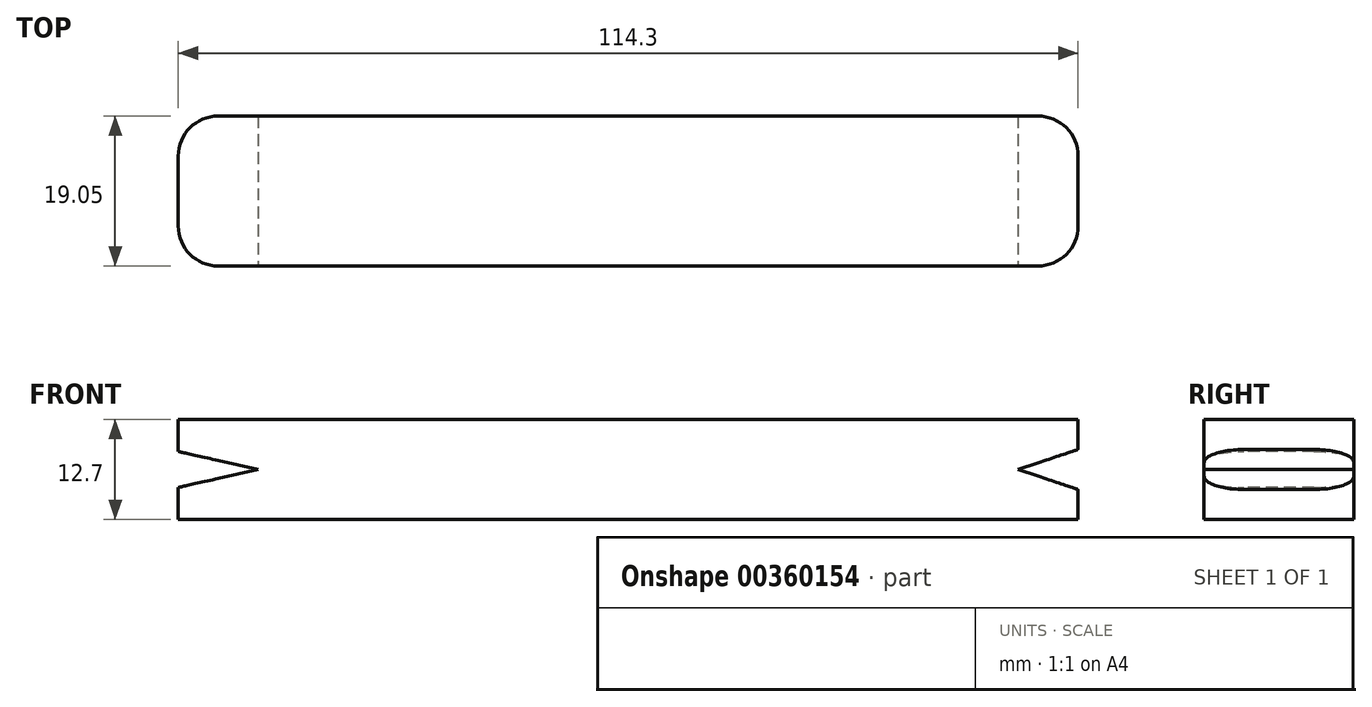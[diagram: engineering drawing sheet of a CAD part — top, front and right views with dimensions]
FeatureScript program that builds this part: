
annotation { "Feature Type Name" : "Feature", "Feature Type Description" : "" }
export const myFeature = defineFeature(function(context is Context, id is Id, definition is map)
    precondition{}
    {
        {
            var Q0;
            Q0=qCreatedBy(makeId("Front.planeOp"),FACE);
            var sketch = newSketch(context, id + "F0", { "sketchPlane" : qUnion([Q0])});
            skLineSegment(sketch, "E0.bottom", {"start": v(0, 0) * mm, "end": v(114.3, 0) * mm});
            skLineSegment(sketch, "E0.top", {"start": v(0, 12.7) * mm, "end": v(114.3, 12.7) * mm});
            skLineSegment(sketch, "E0.left", {"start": v(0, 0) * mm, "end": v(0, 12.7) * mm});
            skLineSegment(sketch, "E0.right", {"start": v(114.3, 0) * mm, "end": v(114.3, 12.7) * mm});
            skLineSegment(sketch, "E1", {"start": v(0, 6.35) * mm, "end": v(114.3, 6.35) * mm, "construction": true});
            skSolve(sketch);
        }
        {
            var Q0;
            Q0=makeQuery(id+"F0.imprint","IMPRINT",FACE,{"disambiguationData":[TD([[makeQuery(id+"F0.imprint","IMPRINT",EDGE,{"derivedFrom":sQuery(id+"F0.wireOp",EDGE,"E0.bottom")}),1.0]])]});
            extrude(context, id + "F1", {"entities" : qUnion([Q0]), "oppositeDirection" : true, "depth" : 19.05 * mm});
        }
        {
            var Q0;
            Q0=makeQuery(id+"F1.opExtrude","CAP_FACE",FACE,{"disambiguationData":[OSD([sQuery(id+"F0.wireOp",EDGE,"E0.bottom"),sQuery(id+"F0.wireOp",EDGE,"E0.top"),sQuery(id+"F0.wireOp",EDGE,"E0.left"),sQuery(id+"F0.wireOp",EDGE,"E0.right")])],"isStart":true});
            var sketch = newSketch(context, id + "F2", { "sketchPlane" : qUnion([Q0])});
            skLineSegment(sketch, "E2", {"start": v(0, 12.7) * mm, "end": v(0, 8.64) * mm, "construction": true});
            skLineSegment(sketch, "E3", {"start": v(0, 0) * mm, "end": v(0, 4.06) * mm, "construction": true});
            skLineSegment(sketch, "E4", {"start": v(0, 6.35) * mm, "end": v(10.16, 6.35) * mm, "construction": true});
            skLineSegment(sketch, "E5", {"start": v(0, 8.64) * mm, "end": v(10.16, 6.35) * mm});
            skLineSegment(sketch, "E6", {"start": v(0, 4.06) * mm, "end": v(10.16, 6.35) * mm});
            skLineSegment(sketch, "E7", {"start": v(114.3, 12.7) * mm, "end": v(114.3, 8.9) * mm, "construction": true});
            skLineSegment(sketch, "E8", {"start": v(114.3, 0) * mm, "end": v(114.3, 3.81) * mm, "construction": true});
            skLineSegment(sketch, "E9", {"start": v(114.3, 6.35) * mm, "end": v(106.68, 6.35) * mm, "construction": true});
            skLineSegment(sketch, "E10", {"start": v(114.3, 8.9) * mm, "end": v(106.68, 6.35) * mm});
            skLineSegment(sketch, "E11", {"start": v(114.3, 3.8) * mm, "end": v(106.68, 6.35) * mm});
            skSolve(sketch);
        }
        {
            var Q0;
            Q0=makeQuery(id+"F1.opExtrude","CAP_EDGE",EDGE,{"disambiguationData":[OSD([sQuery(id+"F0.wireOp",EDGE,"E0.left")])],"isStart":true});
            fillet(context, id + "F3", {"entities" : qUnion([Q0]), "radius" : 5.08 * mm, "tangentPropagation" : true, "allowEdgeOverflow" : false});
        }
        {
            var Q0;
            {var subQ0=sQuery(id+"F2.wireOp",EDGE,"E5");Q0=makeQuery(id+"F2.imprint","IMPRINT",FACE,{"disambiguationData":[TD([[makeQuery(id+"F2.imprint","IMPRINT",EDGE,{"derivedFrom":subQ0}),-1.0]])]});}
            extrude(context, id + "F4", {"entities" : qUnion([Q0]), "operationType" : NewBodyOperationType.REMOVE, "oppositeDirection" : true, "depth" : 19.05 * mm});
        }
        {
            var Q0;
            {var subQ0=sQuery(id+"F0.wireOp",EDGE,"E0.left");var subQ1=sQuery(id+"F0.wireOp",EDGE,"E0.top");Q0=makeQuery(id+"F4.boolean.opBoolean","SPLIT",EDGE,{"disambiguationData":[TD([makeQuery(id+"F1.opExtrude","SWEPT_FACE",FACE,{"disambiguationData":[OSD([subQ1])]})])],"derivedFrom":makeQuery(id+"F1.opExtrude","CAP_EDGE",EDGE,{"disambiguationData":[OSD([subQ0])],"isStart":false})});}
            var Q1;
            {var subQ0=sQuery(id+"F0.wireOp",EDGE,"E0.bottom");var subQ1=sQuery(id+"F0.wireOp",EDGE,"E0.left");Q1=makeQuery(id+"F4.boolean.opBoolean","SPLIT",EDGE,{"disambiguationData":[TD([makeQuery(id+"F1.opExtrude","SWEPT_FACE",FACE,{"disambiguationData":[OSD([subQ0])]})])],"derivedFrom":makeQuery(id+"F1.opExtrude","CAP_EDGE",EDGE,{"disambiguationData":[OSD([subQ1])],"isStart":false})});}
            fillet(context, id + "F5", {"entities" : qUnion([Q0, Q1]), "radius" : 5.08 * mm, "tangentPropagation" : true, "allowEdgeOverflow" : false});
        }
        {
            var Q0;
            Q0=makeQuery(id+"F1.opExtrude","CAP_FACE",FACE,{"disambiguationData":[OSD([sQuery(id+"F0.wireOp",EDGE,"E0.bottom"),sQuery(id+"F0.wireOp",EDGE,"E0.top"),sQuery(id+"F0.wireOp",EDGE,"E0.left"),sQuery(id+"F0.wireOp",EDGE,"E0.right")])],"isStart":true});
            var sketch = newSketch(context, id + "F6", { "sketchPlane" : qUnion([Q0])});
            skLineSegment(sketch, "E12", {"start": v(114.3, 12.7) * mm, "end": v(114.3, 8.9) * mm, "construction": true});
            skLineSegment(sketch, "E13", {"start": v(114.3, 0) * mm, "end": v(114.3, 3.81) * mm, "construction": true});
            skLineSegment(sketch, "E14", {"start": v(114.3, 6.35) * mm, "end": v(106.68, 6.35) * mm, "construction": true});
            skLineSegment(sketch, "E15", {"start": v(114.3, 8.9) * mm, "end": v(106.68, 6.35) * mm});
            skLineSegment(sketch, "E16", {"start": v(106.68, 6.35) * mm, "end": v(114.3, 3.8) * mm});
            skSolve(sketch);
        }
        {
            var Q0;
            {var subQ0=sQuery(id+"F6.wireOp",EDGE,"E15");Q0=makeQuery(id+"F6.imprint","IMPRINT",FACE,{"disambiguationData":[TD([[makeQuery(id+"F6.imprint","IMPRINT",EDGE,{"derivedFrom":subQ0}),1.0]])]});}
            extrude(context, id + "F7", {"entities" : qUnion([Q0]), "operationType" : NewBodyOperationType.REMOVE, "oppositeDirection" : true, "depth" : 25.4 * mm});
        }
        {
            var Q0;
            {var subQ0=sQuery(id+"F0.wireOp",EDGE,"E0.right");var subQ1=sQuery(id+"F0.wireOp",EDGE,"E0.top");Q0=makeQuery(id+"F7.boolean.opBoolean","SPLIT",EDGE,{"disambiguationData":[TD([makeQuery(id+"F1.opExtrude","SWEPT_FACE",FACE,{"disambiguationData":[OSD([subQ1])]})])],"derivedFrom":makeQuery(id+"F1.opExtrude","CAP_EDGE",EDGE,{"disambiguationData":[OSD([subQ0])],"isStart":true})});}
            var Q1;
            {var subQ0=sQuery(id+"F0.wireOp",EDGE,"E0.bottom");var subQ1=sQuery(id+"F0.wireOp",EDGE,"E0.right");Q1=makeQuery(id+"F7.boolean.opBoolean","SPLIT",EDGE,{"disambiguationData":[TD([makeQuery(id+"F1.opExtrude","SWEPT_FACE",FACE,{"disambiguationData":[OSD([subQ0])]})])],"derivedFrom":makeQuery(id+"F1.opExtrude","CAP_EDGE",EDGE,{"disambiguationData":[OSD([subQ1])],"isStart":true})});}
            var Q2;
            {var subQ0=sQuery(id+"F0.wireOp",EDGE,"E0.right");var subQ1=sQuery(id+"F0.wireOp",EDGE,"E0.top");Q2=makeQuery(id+"F7.boolean.opBoolean","SPLIT",EDGE,{"disambiguationData":[TD([makeQuery(id+"F1.opExtrude","SWEPT_FACE",FACE,{"disambiguationData":[OSD([subQ1])]})])],"derivedFrom":makeQuery(id+"F1.opExtrude","CAP_EDGE",EDGE,{"disambiguationData":[OSD([subQ0])],"isStart":false})});}
            var Q3;
            {var subQ0=sQuery(id+"F0.wireOp",EDGE,"E0.bottom");var subQ1=sQuery(id+"F0.wireOp",EDGE,"E0.right");Q3=makeQuery(id+"F7.boolean.opBoolean","SPLIT",EDGE,{"disambiguationData":[TD([makeQuery(id+"F1.opExtrude","SWEPT_FACE",FACE,{"disambiguationData":[OSD([subQ0])]})])],"derivedFrom":makeQuery(id+"F1.opExtrude","CAP_EDGE",EDGE,{"disambiguationData":[OSD([subQ1])],"isStart":false})});}
            fillet(context, id + "F8", {"entities" : qUnion([Q0, Q1, Q2, Q3]), "radius" : 5.08 * mm, "tangentPropagation" : true, "allowEdgeOverflow" : false});
        }
    });
